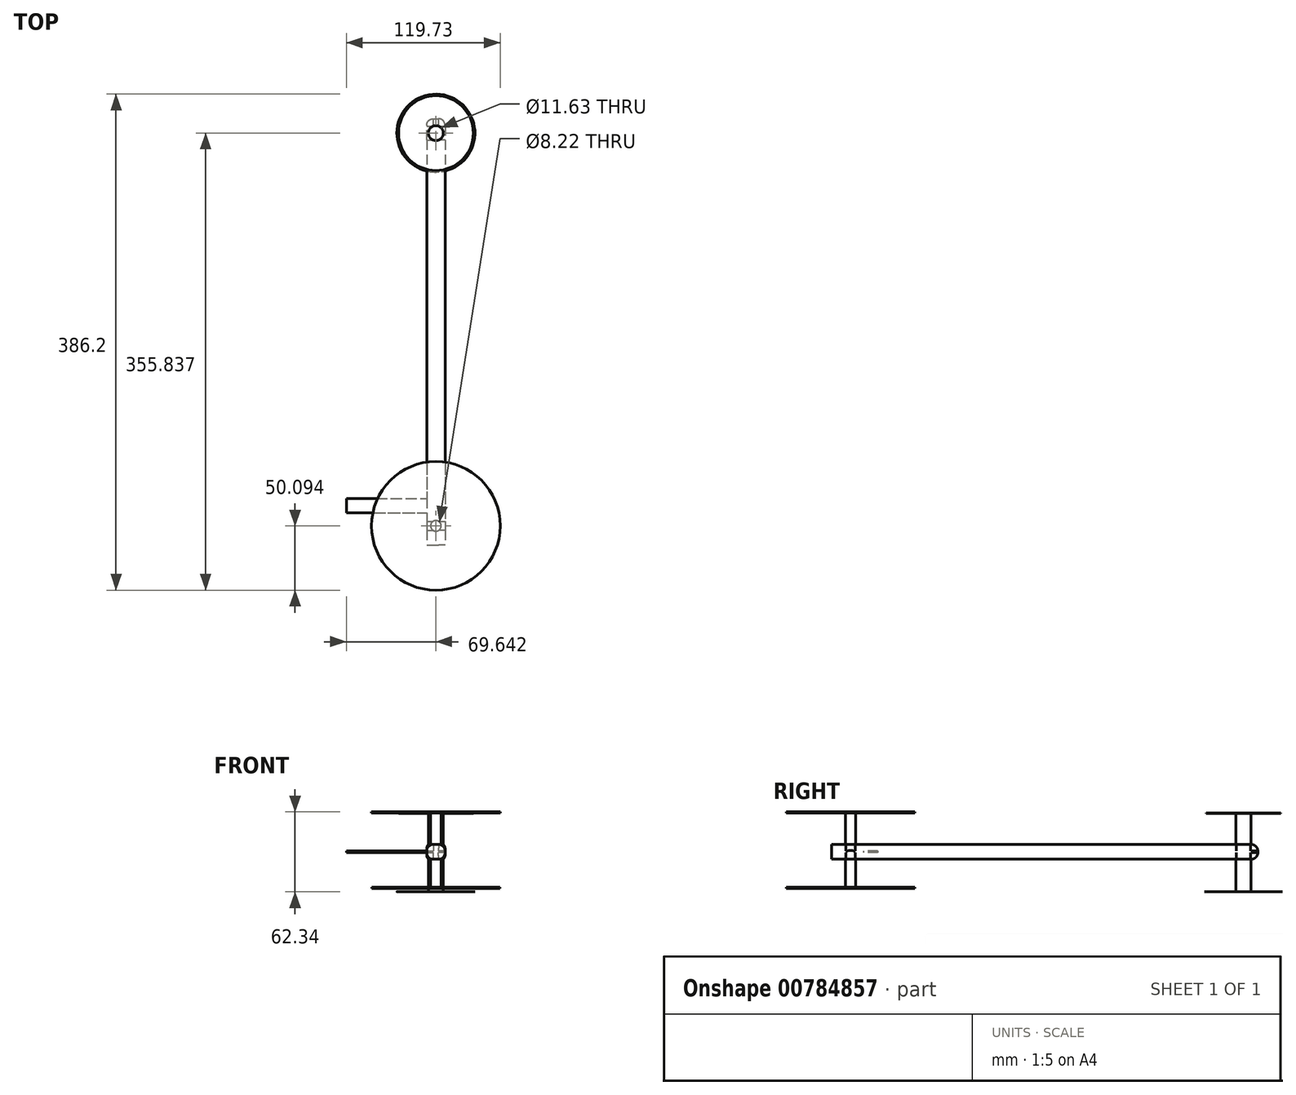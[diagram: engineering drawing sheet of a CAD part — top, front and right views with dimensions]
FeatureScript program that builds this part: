
annotation { "Feature Type Name" : "Feature", "Feature Type Description" : "" }
export const myFeature = defineFeature(function(context is Context, id is Id, definition is map)
    precondition{}
    {
        {
            var Q0;
            Q0=qCreatedBy(makeId("Top.planeOp"),FACE);
            var sketch = newSketch(context, id + "F0", { "sketchPlane" : qUnion([Q0])});
            skLineSegment(sketch, "E0.bottom", {"start": v(0, 153.36) * mm, "end": v(14.3, 153.36) * mm});
            skLineSegment(sketch, "E0.top", {"start": v(0, -178.43) * mm, "end": v(14.3, -178.43) * mm});
            skLineSegment(sketch, "E0.left", {"start": v(0, 153.36) * mm, "end": v(0, -178.43) * mm});
            skLineSegment(sketch, "E0.right", {"start": v(14.3, 153.36) * mm, "end": v(14.3, -178.43) * mm});
            skSolve(sketch);
        }
        {
            var Q0;
            Q0=makeQuery(id+"F0.imprint","IMPRINT",FACE,{"disambiguationData":[TD([[makeQuery(id+"F0.imprint","IMPRINT",EDGE,{"derivedFrom":sQuery(id+"F0.wireOp",EDGE,"E0.bottom")}),-1.0]])]});
            extrude(context, id + "F1", {"entities" : qUnion([Q0]), "depth" : 11.54 * mm, "offsetDistance" : 25.4 * mm});
        }
        {
            var Q0;
            Q0=makeQuery(id+"F1.opExtrude","CAP_FACE",FACE,{"disambiguationData":[OSD([sQuery(id+"F0.wireOp",EDGE,"E0.bottom"),sQuery(id+"F0.wireOp",EDGE,"E0.top"),sQuery(id+"F0.wireOp",EDGE,"E0.left"),sQuery(id+"F0.wireOp",EDGE,"E0.right")])],"isStart":false});
            var sketch = newSketch(context, id + "F2", { "sketchPlane" : qUnion([Q0])});
            skCircle(sketch, "E1", {"center": v(7.15, -163.59) * mm, "radius": 4.1 * mm});
            skPoint(sketch, "E1.centerSnap0", {"position": v(7.15, -178.43) * mm});
            skSolve(sketch);
        }
        {
            var Q0;
            Q0=makeQuery(id+"F2.imprint","IMPRINT",FACE,{"disambiguationData":[TD([[makeQuery(id+"F2.imprint","IMPRINT",EDGE,{"derivedFrom":sQuery(id+"F2.wireOp",EDGE,"E1")}),1.0]])]});
            var Q1;
            Q1 = qSketchRegion(id + "F2", true);
            extrude(context, id + "F3", {"entities" : qUnion([Q0, Q1]), "operationType" : NewBodyOperationType.ADD, "depth" : 25.4 * mm, "offsetDistance" : 25.4 * mm});
        }
        {
            var Q0;
            Q0=makeQuery(id+"F3.opExtrude","CAP_FACE",FACE,{"disambiguationData":[OSD([sQuery(id+"F2.wireOp",EDGE,"E1")])],"isStart":false});
            extrude(context, id + "F4", {"entities" : qUnion([Q0]), "operationType" : NewBodyOperationType.ADD, "oppositeDirection" : true, "depth" : 58.73 * mm, "offsetDistance" : 25.4 * mm});
        }
        {
            var Q0;
            Q0=makeQuery(id+"F4.opExtrude","CAP_FACE",FACE,{"disambiguationData":[OSD([sQuery(id+"F2.wireOp",EDGE,"E1")])],"isStart":false});
            var sketch = newSketch(context, id + "F5", { "sketchPlane" : qUnion([Q0])});
            skCircle(sketch, "E2", {"center": v(7.15, 163.59) * mm, "radius": 49.96 * mm});
            skSolve(sketch);
        }
        {
            var Q0;
            Q0=makeQuery(id+"F3.opExtrude","CAP_FACE",FACE,{"disambiguationData":[OSD([sQuery(id+"F2.wireOp",EDGE,"E1")])],"isStart":false});
            var sketch = newSketch(context, id + "F6", { "sketchPlane" : qUnion([Q0])});
            skCircle(sketch, "E3", {"center": v(7.15, -163.59) * mm, "radius": 50.1 * mm});
            skSolve(sketch);
        }
        {
            var Q0;
            Q0=makeQuery(id+"F5.imprint","IMPRINT",FACE,{"disambiguationData":[TD([[makeQuery(id+"F5.imprint","IMPRINT",EDGE,{"derivedFrom":sQuery(id+"F5.wireOp",EDGE,"E2")}),1.0]])]});
            var Q1;
            Q1=makeQuery(id+"F6.imprint","IMPRINT",FACE,{"disambiguationData":[TD([[makeQuery(id+"F6.imprint","IMPRINT",EDGE,{"derivedFrom":sQuery(id+"F6.wireOp",EDGE,"E3")}),1.0]])]});
            extrude(context, id + "F7", {"entities" : qUnion([Q0, Q1]), "operationType" : NewBodyOperationType.ADD, "depth" : 0.91 * mm, "offsetDistance" : 25.4 * mm});
        }
        {
            var Q0;
            Q0=makeQuery(id+"F1.opExtrude","CAP_FACE",FACE,{"disambiguationData":[OSD([sQuery(id+"F0.wireOp",EDGE,"E0.bottom"),sQuery(id+"F0.wireOp",EDGE,"E0.top"),sQuery(id+"F0.wireOp",EDGE,"E0.left"),sQuery(id+"F0.wireOp",EDGE,"E0.right")])],"isStart":true});
            var sketch = newSketch(context, id + "F8", { "sketchPlane" : qUnion([Q0])});
            skCircle(sketch, "E4", {"center": v(7.15, -142.16) * mm, "radius": 5.81 * mm});
            skPoint(sketch, "E4.centerSnap0", {"position": v(7.15, -153.36) * mm});
            skSolve(sketch);
        }
        {
            var Q0;
            Q0=makeQuery(id+"F8.imprint","IMPRINT",FACE,{"disambiguationData":[TD([[makeQuery(id+"F8.imprint","IMPRINT",EDGE,{"derivedFrom":sQuery(id+"F8.wireOp",EDGE,"E4")}),1.0]])]});
            extrude(context, id + "F9", {"entities" : qUnion([Q0]), "operationType" : NewBodyOperationType.ADD, "depth" : 25.4 * mm, "offsetDistance" : 25.4 * mm});
        }
        {
            var Q0;
            Q0=makeQuery(id+"F9.opExtrude","CAP_FACE",FACE,{"disambiguationData":[OSD([sQuery(id+"F8.wireOp",EDGE,"E4")])],"isStart":false});
            extrude(context, id + "F10", {"entities" : qUnion([Q0]), "operationType" : NewBodyOperationType.ADD, "oppositeDirection" : true, "depth" : 61 * mm, "offsetDistance" : 25.4 * mm});
        }
        {
            var Q0;
            Q0=makeQuery(id+"F9.opExtrude","CAP_FACE",FACE,{"disambiguationData":[OSD([sQuery(id+"F8.wireOp",EDGE,"E4")])],"isStart":false});
            var sketch = newSketch(context, id + "F11", { "sketchPlane" : qUnion([Q0])});
            skCircle(sketch, "E5", {"center": v(7.15, -142.16) * mm, "radius": 30.36 * mm});
            skSolve(sketch);
        }
        {
            var Q0;
            Q0=makeQuery(id+"F10.opExtrude","CAP_FACE",FACE,{"disambiguationData":[OSD([sQuery(id+"F8.wireOp",EDGE,"E4")])],"isStart":false});
            var sketch = newSketch(context, id + "F12", { "sketchPlane" : qUnion([Q0])});
            skCircle(sketch, "E6", {"center": v(7.15, 142.16) * mm, "radius": 29.09 * mm});
            skSolve(sketch);
        }
        {
            var Q0;
            Q0=makeQuery(id+"F12.imprint","IMPRINT",FACE,{"disambiguationData":[TD([[makeQuery(id+"F12.imprint","IMPRINT",EDGE,{"derivedFrom":sQuery(id+"F12.wireOp",EDGE,"E6")}),1.0]])]});
            var Q1;
            Q1=makeQuery(id+"F11.imprint","IMPRINT",FACE,{"disambiguationData":[TD([[makeQuery(id+"F11.imprint","IMPRINT",EDGE,{"derivedFrom":sQuery(id+"F11.wireOp",EDGE,"E5")}),1.0]])]});
            extrude(context, id + "F13", {"entities" : qUnion([Q0, Q1]), "operationType" : NewBodyOperationType.ADD, "depth" : 0.25 * mm, "offsetDistance" : 25.4 * mm});
        }
        {
            var Q0;
            Q0=makeQuery(id+"F1.opExtrude","CAP_EDGE",EDGE,{"disambiguationData":[OSD([sQuery(id+"F0.wireOp",EDGE,"E0.left")])],"isStart":true});
            var Q1;
            Q1=makeQuery(id+"F1.opExtrude","CAP_EDGE",EDGE,{"disambiguationData":[OSD([sQuery(id+"F0.wireOp",EDGE,"E0.right")])],"isStart":false});
            var Q2;
            Q2=makeQuery(id+"F1.opExtrude","CAP_EDGE",EDGE,{"disambiguationData":[OSD([sQuery(id+"F0.wireOp",EDGE,"E0.right")])],"isStart":true});
            var Q3;
            Q3=makeQuery(id+"F1.opExtrude","CAP_EDGE",EDGE,{"disambiguationData":[OSD([sQuery(id+"F0.wireOp",EDGE,"E0.left")])],"isStart":false});
            fillet(context, id + "F14", {"entities" : qUnion([Q0, Q1, Q2, Q3]), "radius" : 5.08 * mm, "tangentPropagation" : true, "allowEdgeOverflow" : false});
        }
        {
            var Q0;
            Q0=makeQuery(id+"F14.opFillet","BLEND_EDGE",EDGE,{"blendedFrom":[makeQuery(id+"F1.opExtrude","CAP_EDGE",EDGE,{"disambiguationData":[OSD([sQuery(id+"F0.wireOp",EDGE,"E0.left")])],"isStart":false}),makeQuery(id+"F1.opExtrude","SWEPT_FACE",FACE,{"disambiguationData":[OSD([sQuery(id+"F0.wireOp",EDGE,"E0.bottom")])]})],"blendedInto":[makeQuery(id+"F1.opExtrude","SWEPT_FACE",FACE,{"disambiguationData":[OSD([sQuery(id+"F0.wireOp",EDGE,"E0.bottom")])]})]});
            var Q1;
            Q1=makeQuery(id+"F1.opExtrude","CAP_EDGE",EDGE,{"disambiguationData":[OSD([sQuery(id+"F0.wireOp",EDGE,"E0.bottom")])],"isStart":false});
            var Q2;
            Q2=makeQuery(id+"F14.opFillet","BLEND_EDGE",EDGE,{"blendedFrom":[makeQuery(id+"F1.opExtrude","CAP_EDGE",EDGE,{"disambiguationData":[OSD([sQuery(id+"F0.wireOp",EDGE,"E0.left")])],"isStart":true}),makeQuery(id+"F1.opExtrude","SWEPT_FACE",FACE,{"disambiguationData":[OSD([sQuery(id+"F0.wireOp",EDGE,"E0.bottom")])]})],"blendedInto":[makeQuery(id+"F1.opExtrude","SWEPT_FACE",FACE,{"disambiguationData":[OSD([sQuery(id+"F0.wireOp",EDGE,"E0.bottom")])]})]});
            fillet(context, id + "F15", {"entities" : qUnion([Q0, Q1, Q2]), "radius" : 5.16 * mm, "tangentPropagation" : true, "allowEdgeOverflow" : false});
        }
        {
            var Q0;
            Q0=makeQuery(id+"F1.opExtrude","SWEPT_FACE",FACE,{"disambiguationData":[OSD([sQuery(id+"F0.wireOp",EDGE,"E0.left")])]});
            var sketch = newSketch(context, id + "F16", { "sketchPlane" : qUnion([Q0])});
            skLineSegment(sketch, "E7.bottom", {"start": v(153.45, 6.46) * mm, "end": v(142.47, 6.46) * mm});
            skLineSegment(sketch, "E7.top", {"start": v(153.45, 5.08) * mm, "end": v(142.47, 5.08) * mm});
            skLineSegment(sketch, "E7.left", {"start": v(153.45, 6.46) * mm, "end": v(153.45, 5.08) * mm});
            skLineSegment(sketch, "E7.right", {"start": v(142.47, 6.46) * mm, "end": v(142.47, 5.08) * mm});
            skSolve(sketch);
        }
        {
            var Q0;
            Q0=makeQuery(id+"F16.imprint","IMPRINT",FACE,{"disambiguationData":[TD([[makeQuery(id+"F16.imprint","IMPRINT",EDGE,{"derivedFrom":sQuery(id+"F16.wireOp",EDGE,"E7.bottom")}),1.0]])]});
            extrude(context, id + "F17", {"entities" : qUnion([Q0]), "operationType" : NewBodyOperationType.ADD, "depth" : 62.5 * mm, "offsetDistance" : 25.4 * mm});
        }
    });
